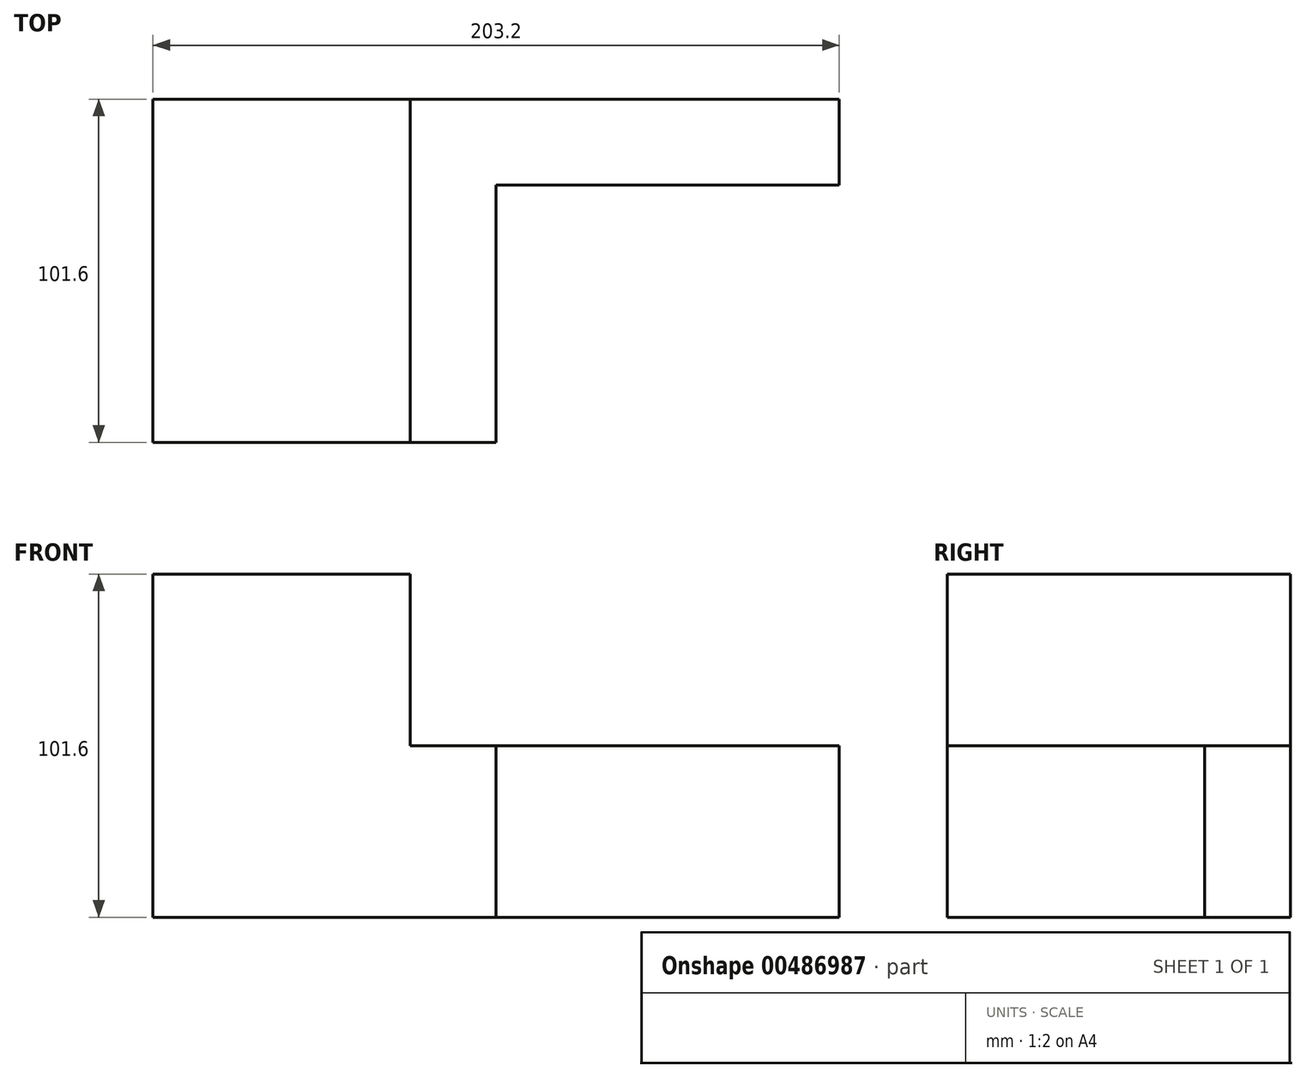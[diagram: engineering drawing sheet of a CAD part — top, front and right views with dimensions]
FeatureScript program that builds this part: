
annotation { "Feature Type Name" : "Feature", "Feature Type Description" : "" }
export const myFeature = defineFeature(function(context is Context, id is Id, definition is map)
    precondition{}
    {
        {
            var Q0;
            Q0=qCreatedBy(makeId("Top.planeOp"),FACE);
            var sketch = newSketch(context, id + "F0", { "sketchPlane" : qUnion([Q0])});
            skLineSegment(sketch, "E0.bottom", {"start": v(-58.78, 46.54) * mm, "end": v(42.82, 46.54) * mm});
            skLineSegment(sketch, "E0.top", {"start": v(-58.78, -29.66) * mm, "end": v(42.82, -29.66) * mm});
            skLineSegment(sketch, "E0.left", {"start": v(-58.78, 46.54) * mm, "end": v(-58.78, -29.66) * mm});
            skLineSegment(sketch, "E0.right", {"start": v(42.82, 46.54) * mm, "end": v(42.82, -29.66) * mm});
            skSolve(sketch);
        }
        {
            var Q0;
            Q0 = qSketchRegion(id + "F0", true);
            var Q1;
            Q1 = qSketchRegion(id + "F2", true);
            extrude(context, id + "F1", {"entities" : qUnion([Q0, Q1]), "depth" : 101.6 * mm});
        }
        {
            var Q0;
            Q0=qCreatedBy(makeId("Top.planeOp"),FACE);
            var sketch = newSketch(context, id + "F2", { "sketchPlane" : qUnion([Q0])});
            skLineSegment(sketch, "E1.bottom", {"start": v(-7.98, -29.66) * mm, "end": v(-58.78, -29.66) * mm});
            skLineSegment(sketch, "E1.top", {"start": v(-7.98, -55.06) * mm, "end": v(-58.78, -55.06) * mm});
            skLineSegment(sketch, "E1.left", {"start": v(-7.98, -29.66) * mm, "end": v(-7.98, -55.06) * mm});
            skLineSegment(sketch, "E1.right", {"start": v(-58.78, -29.66) * mm, "end": v(-58.78, -55.06) * mm});
            skSolve(sketch);
        }
        {
            var Q0;
            Q0=makeQuery(id+"F2.imprint","IMPRINT",FACE,{"disambiguationData":[TD([[makeQuery(id+"F2.imprint","IMPRINT",EDGE,{"derivedFrom":sQuery(id+"F2.wireOp",EDGE,"E1.bottom")}),1.0]])]});
            extrude(context, id + "F3", {"entities" : qUnion([Q0]), "operationType" : NewBodyOperationType.ADD, "depth" : 101.6 * mm});
        }
        {
            var Q0;
            Q0=qCreatedBy(makeId("Top.planeOp"),FACE);
            var sketch = newSketch(context, id + "F4", { "sketchPlane" : qUnion([Q0])});
            skLineSegment(sketch, "E2.bottom", {"start": v(-7.98, -55.06) * mm, "end": v(-58.78, -55.06) * mm});
            skLineSegment(sketch, "E2.top", {"start": v(-7.98, -156.66) * mm, "end": v(-58.78, -156.66) * mm});
            skLineSegment(sketch, "E2.left", {"start": v(-7.98, -55.06) * mm, "end": v(-7.98, -156.66) * mm});
            skLineSegment(sketch, "E2.right", {"start": v(-58.78, -55.06) * mm, "end": v(-58.78, -156.66) * mm});
            skSolve(sketch);
        }
        {
            var Q0;
            Q0=makeQuery(id+"F4.imprint","IMPRINT",FACE,{"disambiguationData":[TD([[makeQuery(id+"F4.imprint","IMPRINT",EDGE,{"derivedFrom":sQuery(id+"F4.wireOp",EDGE,"E2.bottom")}),1.0]])]});
            extrude(context, id + "F5", {"entities" : qUnion([Q0]), "operationType" : NewBodyOperationType.ADD, "depth" : 25.4 * mm});
        }
        {
            var Q0;
            Q0=makeQuery(id+"F1.opExtrude","SWEPT_BODY",BODY,{"disambiguationData":[OSD([sQuery(id+"F0.wireOp",EDGE,"E0.bottom"),sQuery(id+"F0.wireOp",EDGE,"E0.top"),sQuery(id+"F0.wireOp",EDGE,"E0.left"),sQuery(id+"F0.wireOp",EDGE,"E0.right")])]});
            var Q1;
            Q1=makeQuery(id+"F3.boolean.opBoolean","MERGE",EDGE,{"derivedFrom":[makeQuery(id+"F1.opExtrude","CAP_EDGE",EDGE,{"disambiguationData":[OSD([sQuery(id+"F0.wireOp",EDGE,"E0.left")])],"isStart":false}),makeQuery(id+"F3.opExtrude","CAP_EDGE",EDGE,{"disambiguationData":[OSD([sQuery(id+"F2.wireOp",EDGE,"E1.right")])],"isStart":false})]});
            transform(context, id + "F6", {"entities" : qUnion([Q0]), "transformType" : TransformType.ROTATION, "transformAxis" : qUnion([Q1]), "angle" : 90 * degree, "makeCopy" : false});
        }
        {
            var Q0;
            Q0=makeQuery(id+"F1.opExtrude","SWEPT_BODY",BODY,{"disambiguationData":[OSD([sQuery(id+"F0.wireOp",EDGE,"E0.bottom"),sQuery(id+"F0.wireOp",EDGE,"E0.top"),sQuery(id+"F0.wireOp",EDGE,"E0.left"),sQuery(id+"F0.wireOp",EDGE,"E0.right")])]});
            var Q1;
            Q1=makeQuery(id+"F5.opExtrude","CAP_EDGE",EDGE,{"disambiguationData":[OSD([sQuery(id+"F4.wireOp",EDGE,"E2.top")])],"isStart":true});
            transform(context, id + "F7", {"entities" : qUnion([Q0]), "transformType" : TransformType.ROTATION, "transformAxis" : qUnion([Q1]), "angle" : 90 * degree, "oppositeDirection" : true, "makeCopy" : false});
        }
    });
